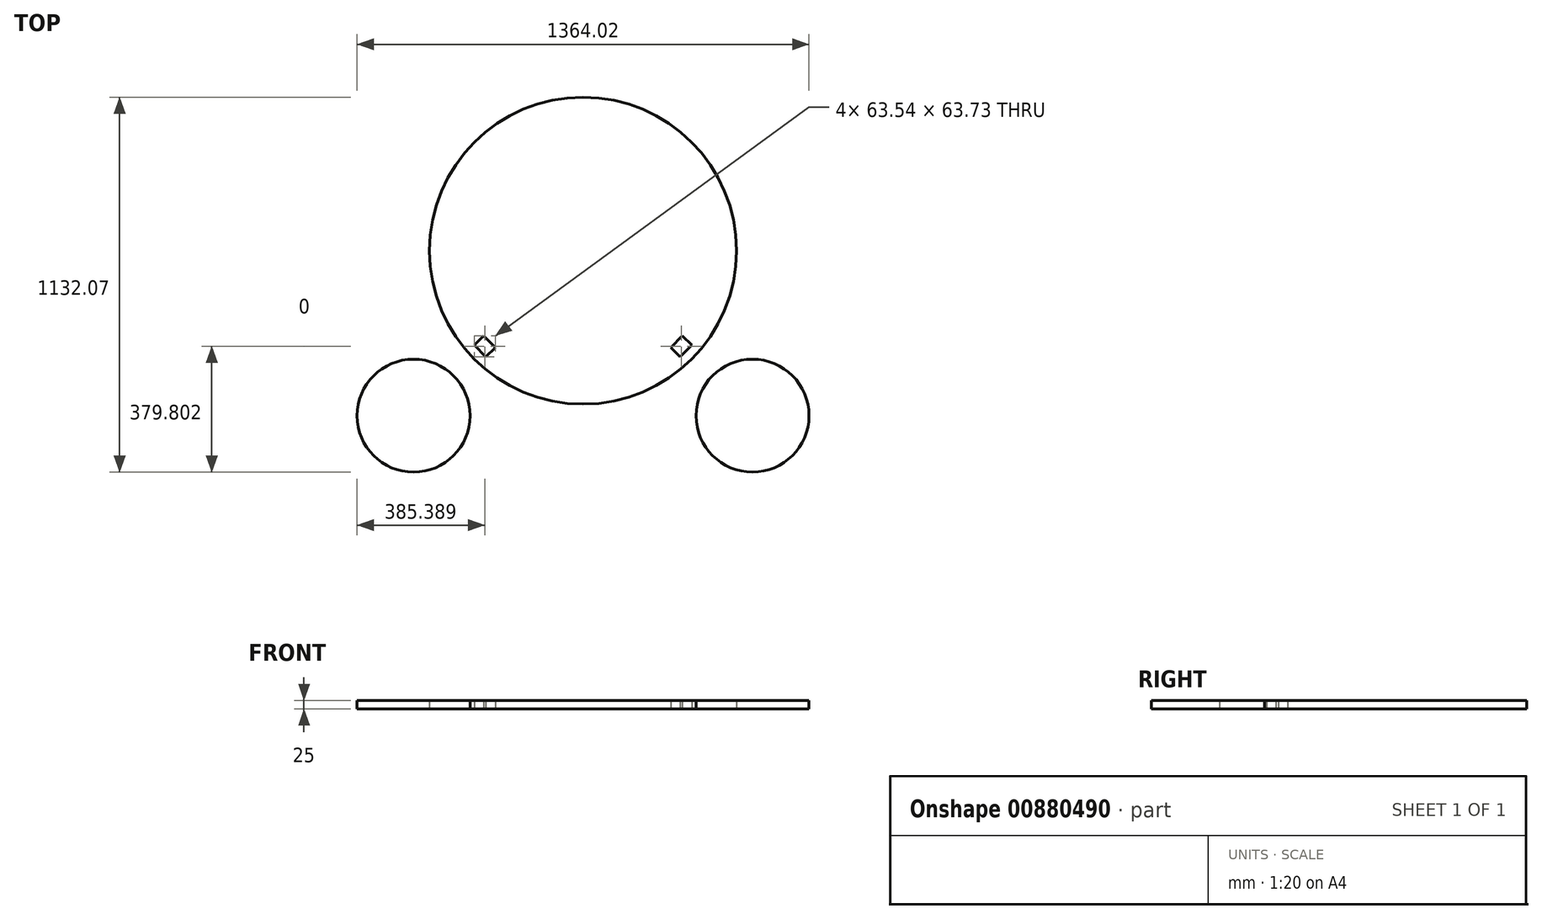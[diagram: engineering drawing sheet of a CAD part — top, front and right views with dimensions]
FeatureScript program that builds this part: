
annotation { "Feature Type Name" : "Feature", "Feature Type Description" : "" }
export const myFeature = defineFeature(function(context is Context, id is Id, definition is map)
    precondition{}
    {
        {
            var Q0;
            Q0=qCreatedBy(makeId("Top.planeOp"),FACE);
            var sketch = newSketch(context, id + "F0", { "sketchPlane" : qUnion([Q0])});
            skArc(sketch, "E0", {"start": v(-85.9, 534.6) * mm, "mid": v(-549.26, 71.25) * mm, "end": v(-85.9, -392.1) * mm});
            skLineSegment(sketch, "E1", {"start": v(-85.9, 71.25) * mm, "end": v(-597.43, -427) * mm, "construction": true});
            skCircle(sketch, "E2", {"center": v(-597.43, -427) * mm, "radius": 170.48 * mm});
            skLineSegment(sketch, "E3", {"start": v(-414.3, -213.71) * mm, "end": v(-379.41, -249.53) * mm});
            skLineSegment(sketch, "E4", {"start": v(-379.41, -249.53) * mm, "end": v(-350.76, -221.62) * mm});
            skLineSegment(sketch, "E5", {"start": v(-350.76, -221.62) * mm, "end": v(-385.65, -185.8) * mm});
            skLineSegment(sketch, "E6", {"start": v(-385.65, -185.8) * mm, "end": v(-414.3, -213.71) * mm});
            skPoint(sketch, "E7", {"position": v(-382.53, -217.67) * mm});
            skLineSegment(sketch, "E8", {"start": v(-85.9, 534.6) * mm, "end": v(-85.9, -392.1) * mm, "construction": true});
            skArc(sketch, "E9.MirrorCS", {"start": v(-85.9, 534.6) * mm, "mid": v(377.44, 71.25) * mm, "end": v(-85.9, -392.1) * mm});
            skLineSegment(sketch, "E10.MirrorCS", {"start": v(-85.9, 71.25) * mm, "end": v(425.62, -427) * mm, "construction": true});
            skCircle(sketch, "E11.MirrorC", {"center": v(425.62, -427) * mm, "radius": 170.48 * mm});
            skLineSegment(sketch, "E12.MirrorCS", {"start": v(207.6, -249.53) * mm, "end": v(178.94, -221.62) * mm});
            skLineSegment(sketch, "E13.MirrorCS", {"start": v(178.94, -221.62) * mm, "end": v(213.83, -185.8) * mm});
            skLineSegment(sketch, "E14.MirrorCS", {"start": v(213.83, -185.8) * mm, "end": v(242.48, -213.71) * mm});
            skLineSegment(sketch, "E15.MirrorCS", {"start": v(242.48, -213.71) * mm, "end": v(207.6, -249.53) * mm});
            skSolve(sketch);
        }
        {
            var Q0;
            Q0 = qSketchRegion(id + "F0", true);
            extrude(context, id + "F1", {"entities" : qUnion([Q0]), "depth" : 25 * mm, "offsetDistance" : 25 * mm});
        }
        {
            var Q0;
            Q0 = qSketchRegion(id + "F0", true);
            extrude(context, id + "F2", {"entities" : qUnion([Q0]), "depth" : 25 * mm, "offsetDistance" : 25 * mm});
        }
    });
